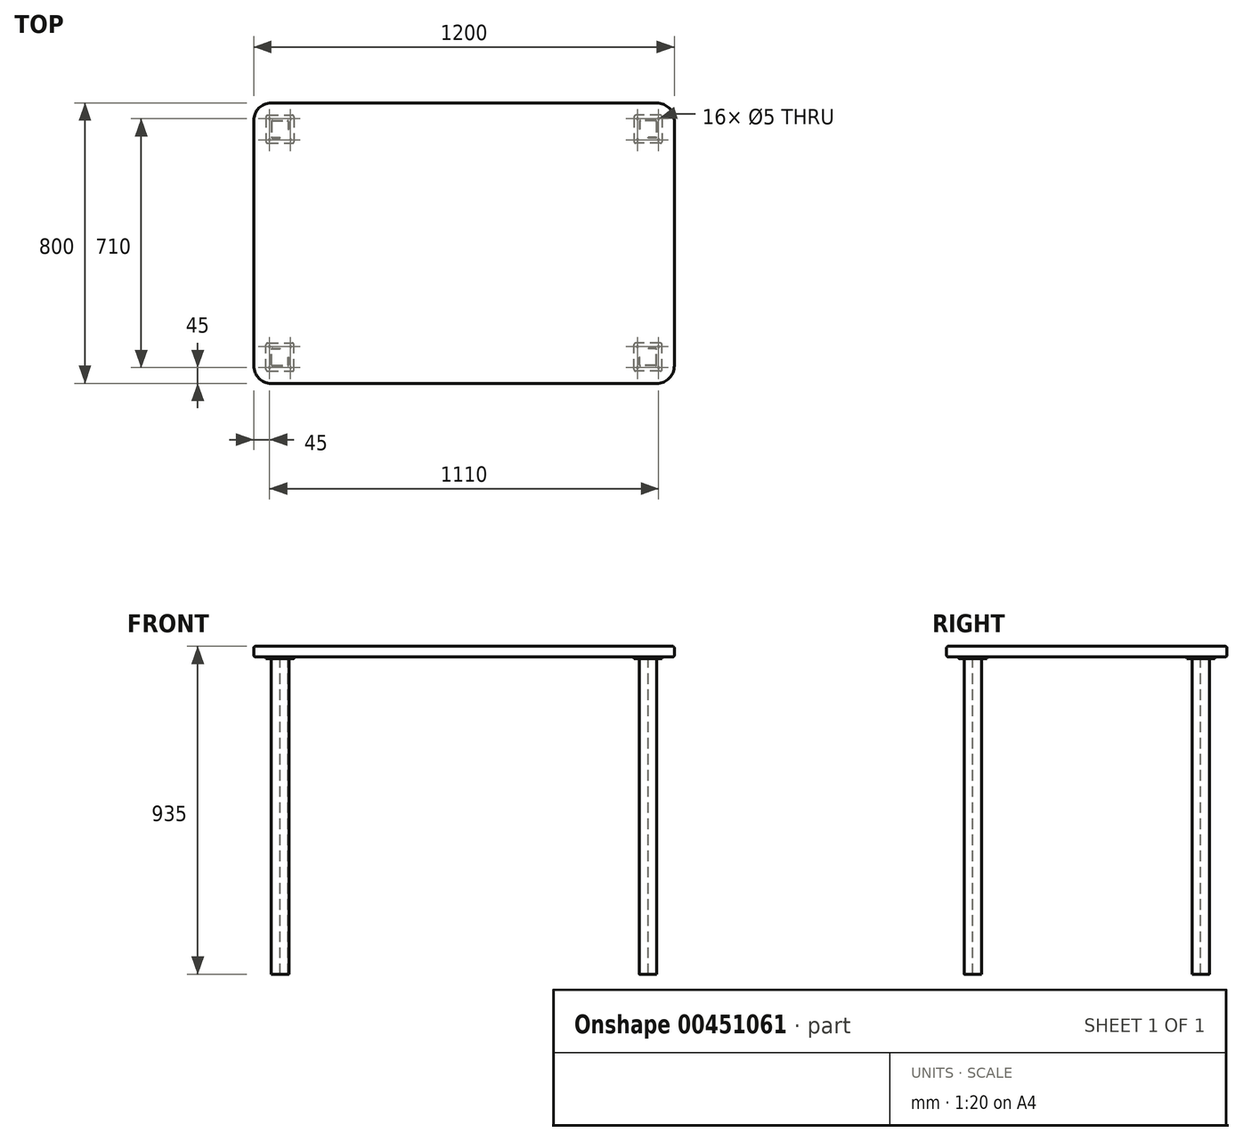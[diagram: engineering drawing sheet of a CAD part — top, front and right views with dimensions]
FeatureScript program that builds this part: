
annotation { "Feature Type Name" : "Feature", "Feature Type Description" : "" }
export const myFeature = defineFeature(function(context is Context, id is Id, definition is map)
    precondition{}
    {
        {
            var Q0;
            Q0=qCreatedBy(makeId("Top.planeOp"),FACE);
            cPlane(context, id + "F0", {"entities" : qUnion([Q0]), "cplaneType" : CPlaneType.OFFSET, "offset" : 5 * mm, "oppositeDirection" : true, "width" : 150 * mm, "height" : 150 * mm});
        }
        {
            var Q0;
            Q0=qCreatedBy(id+"F0.planeOp",FACE);
            var sketch = newSketch(context, id + "F1", { "sketchPlane" : qUnion([Q0])});
            skLineSegment(sketch, "E0.bottom", {"start": v(-546.5, -350) * mm, "end": v(-503.5, -350) * mm});
            skLineSegment(sketch, "E0.top", {"start": v(-546.5, -300) * mm, "end": v(-525, -300) * mm});
            skLineSegment(sketch, "E0.left", {"start": v(-550, -346.5) * mm, "end": v(-550, -303.5) * mm});
            skLineSegment(sketch, "E0.right", {"start": v(-500, -346.5) * mm, "end": v(-500, -325) * mm});
            skPoint(sketch, "E1.endSnap0", {"position": v(-500, -325) * mm});
            skPoint(sketch, "E2.orphan", {"position": v(-500, -300) * mm});
            skPoint(sketch, "E1.start.orphan", {"position": v(-500, -325) * mm});
            skPoint(sketch, "E3.visualSharp", {"position": v(-550, -300) * mm});
            skArc(sketch, "E3.filletArc", {"start": v(-546.5, -300) * mm, "mid": v(-548.97, -301.03) * mm, "end": v(-550, -303.5) * mm});
            skPoint(sketch, "E4.visualSharp", {"position": v(-500, -350) * mm});
            skArc(sketch, "E4.filletArc", {"start": v(-503.5, -350) * mm, "mid": v(-501.03, -348.97) * mm, "end": v(-500, -346.5) * mm});
            skArc(sketch, "E5.filletArc", {"start": v(-550, -346.5) * mm, "mid": v(-548.97, -348.97) * mm, "end": v(-546.5, -350) * mm});
            skLineSegment(sketch, "E6.0", {"start": v(-546.5, -301.5) * mm, "end": v(-525, -301.5) * mm});
            skArc(sketch, "E6.1", {"start": v(-546.5, -301.5) * mm, "mid": v(-547.91, -302.09) * mm, "end": v(-548.5, -303.5) * mm});
            skLineSegment(sketch, "E6.2", {"start": v(-548.5, -346.5) * mm, "end": v(-548.5, -303.5) * mm});
            skLineSegment(sketch, "E6.3", {"start": v(-501.5, -346.5) * mm, "end": v(-501.5, -325) * mm});
            skArc(sketch, "E6.4", {"start": v(-503.5, -348.5) * mm, "mid": v(-502.09, -347.91) * mm, "end": v(-501.5, -346.5) * mm});
            skLineSegment(sketch, "E6.5", {"start": v(-546.5, -348.5) * mm, "end": v(-503.5, -348.5) * mm});
            skArc(sketch, "E6.6", {"start": v(-548.5, -346.5) * mm, "mid": v(-547.91, -347.91) * mm, "end": v(-546.5, -348.5) * mm});
            skLineSegment(sketch, "E7", {"start": v(-525, -300) * mm, "end": v(-525, -301.5) * mm});
            skLineSegment(sketch, "E8", {"start": v(-501.5, -325) * mm, "end": v(-500, -325) * mm});
            skSolve(sketch);
        }
        {
            var Q0;
            Q0 = qSketchRegion(id + "F1", true);
            extrude(context, id + "F2", {"entities" : qUnion([Q0]), "oppositeDirection" : true, "depth" : 900 * mm});
        }
        {
            var Q0;
            Q0=makeQuery(id+"F2.opExtrude","CAP_FACE",FACE,{"disambiguationData":[OSD([sQuery(id+"F1.wireOp",EDGE,"E0.bottom"),sQuery(id+"F1.wireOp",EDGE,"E0.top"),sQuery(id+"F1.wireOp",EDGE,"E0.left"),sQuery(id+"F1.wireOp",EDGE,"E0.right"),sQuery(id+"F1.wireOp",EDGE,"E3.filletArc"),sQuery(id+"F1.wireOp",EDGE,"E4.filletArc"),sQuery(id+"F1.wireOp",EDGE,"E5.filletArc"),sQuery(id+"F1.wireOp",EDGE,"E6.0"),sQuery(id+"F1.wireOp",EDGE,"E6.1"),sQuery(id+"F1.wireOp",EDGE,"E6.2"),sQuery(id+"F1.wireOp",EDGE,"E6.3"),sQuery(id+"F1.wireOp",EDGE,"E6.4"),sQuery(id+"F1.wireOp",EDGE,"E6.5"),sQuery(id+"F1.wireOp",EDGE,"E6.6"),sQuery(id+"F1.wireOp",EDGE,"E7"),sQuery(id+"F1.wireOp",EDGE,"E8")])],"isStart":true});
            var sketch = newSketch(context, id + "F3", { "sketchPlane" : qUnion([Q0])});
            skLineSegment(sketch, "E9.0", {"start": v(-565, -285) * mm, "end": v(-485, -285) * mm});
            skLineSegment(sketch, "E9.2", {"start": v(-565, -365) * mm, "end": v(-565, -285) * mm});
            skLineSegment(sketch, "E9.3", {"start": v(-485, -365) * mm, "end": v(-485, -285) * mm});
            skLineSegment(sketch, "E9.5", {"start": v(-565, -365) * mm, "end": v(-485, -365) * mm});
            skSolve(sketch);
        }
        {
            var Q0;
            Q0 = qSketchRegion(id + "F3", true);
            extrude(context, id + "F4", {"entities" : qUnion([Q0]), "depth" : 5 * mm});
        }
        {
            var Q0;
            Q0=makeQuery(id+"F4.opExtrude","SWEPT_EDGE",EDGE,{"disambiguationData":[OSD([sQuery(id+"F3.wireOp",EDGE,"E9.0"),sQuery(id+"F3.wireOp",EDGE,"E9.2")])]});
            var Q1;
            Q1=makeQuery(id+"F4.opExtrude","SWEPT_EDGE",EDGE,{"disambiguationData":[OSD([sQuery(id+"F3.wireOp",EDGE,"E9.2"),sQuery(id+"F3.wireOp",EDGE,"E9.5")])]});
            var Q2;
            Q2=makeQuery(id+"F4.opExtrude","SWEPT_EDGE",EDGE,{"disambiguationData":[OSD([sQuery(id+"F3.wireOp",EDGE,"E9.3"),sQuery(id+"F3.wireOp",EDGE,"E9.5")])]});
            var Q3;
            Q3=makeQuery(id+"F4.opExtrude","SWEPT_EDGE",EDGE,{"disambiguationData":[OSD([sQuery(id+"F3.wireOp",EDGE,"E9.0"),sQuery(id+"F3.wireOp",EDGE,"E9.3")])]});
            fillet(context, id + "F5", {"entities" : qUnion([Q0, Q1, Q2, Q3]), "radius" : 5 * mm, "tangentPropagation" : true, "allowEdgeOverflow" : false});
        }
        {
            var Q0;
            Q0=makeQuery(id+"F4.opExtrude","CAP_FACE",FACE,{"disambiguationData":[OSD([sQuery(id+"F3.wireOp",EDGE,"E9.0"),sQuery(id+"F3.wireOp",EDGE,"E9.2"),sQuery(id+"F3.wireOp",EDGE,"E9.3"),sQuery(id+"F3.wireOp",EDGE,"E9.5")])],"isStart":false});
            var sketch = newSketch(context, id + "F6", { "sketchPlane" : qUnion([Q0])});
            skLineSegment(sketch, "E10.0", {"start": v(-555, -295) * mm, "end": v(-555, -355) * mm, "construction": true});
            skLineSegment(sketch, "E10.1", {"start": v(-495, -295) * mm, "end": v(-555, -295) * mm, "construction": true});
            skLineSegment(sketch, "E10.2", {"start": v(-495, -355) * mm, "end": v(-495, -295) * mm, "construction": true});
            skLineSegment(sketch, "E10.3", {"start": v(-555, -355) * mm, "end": v(-495, -355) * mm, "construction": true});
            skPoint(sketch, "E11", {"position": v(-555, -355) * mm});
            skPoint(sketch, "E12", {"position": v(-495, -355) * mm});
            skPoint(sketch, "E13", {"position": v(-495, -295) * mm});
            skPoint(sketch, "E14", {"position": v(-555, -295) * mm});
            skSolve(sketch);
        }
        {
            var Q0;
            Q0=sQuery(id+"F6.wireOp",VERTEX,"E11");
            var Q1;
            Q1=sQuery(id+"F6.wireOp",VERTEX,"E12");
            var Q2;
            Q2=sQuery(id+"F6.wireOp",VERTEX,"E13");
            var Q3;
            Q3=sQuery(id+"F6.wireOp",VERTEX,"E14");
            var Q4;
            Q4=makeQuery(id+"F4.opExtrude","SWEPT_BODY",BODY,{"disambiguationData":[OSD([sQuery(id+"F3.wireOp",EDGE,"E9.0"),sQuery(id+"F3.wireOp",EDGE,"E9.2"),sQuery(id+"F3.wireOp",EDGE,"E9.3"),sQuery(id+"F3.wireOp",EDGE,"E9.5")])]});
            hole(context, id + "F7", {"style" : HoleStyle.SIMPLE, "endStyle" : HoleEndStyle.THROUGH, "standardTappedOrClearance" : lookupTablePath({ "standard" : "ISO", "size" : "5", "type" : "Drilled" }), "standardBlindInLast" : lookupTablePath({ "standard" : "ISO", "size" : "5", "type" : "Drilled" }), "holeDiameter" : 5 * mm, "isTappedThrough" : true, "tappedDepth" : 12 * mm, "tapClearance" : 3, "locations" : qUnion([Q0, Q1, Q2, Q3]), "scope" : qUnion([Q4])});
        }
        {
            var Q0;
            Q0=makeQuery(id+"F2.opExtrude","SWEPT_BODY",BODY,{"disambiguationData":[OSD([sQuery(id+"F1.wireOp",EDGE,"E0.bottom"),sQuery(id+"F1.wireOp",EDGE,"E0.top"),sQuery(id+"F1.wireOp",EDGE,"E0.left"),sQuery(id+"F1.wireOp",EDGE,"E0.right"),sQuery(id+"F1.wireOp",EDGE,"E3.filletArc"),sQuery(id+"F1.wireOp",EDGE,"E4.filletArc"),sQuery(id+"F1.wireOp",EDGE,"E5.filletArc"),sQuery(id+"F1.wireOp",EDGE,"E6.0"),sQuery(id+"F1.wireOp",EDGE,"E6.1"),sQuery(id+"F1.wireOp",EDGE,"E6.2"),sQuery(id+"F1.wireOp",EDGE,"E6.3"),sQuery(id+"F1.wireOp",EDGE,"E6.4"),sQuery(id+"F1.wireOp",EDGE,"E6.5"),sQuery(id+"F1.wireOp",EDGE,"E6.6"),sQuery(id+"F1.wireOp",EDGE,"E7"),sQuery(id+"F1.wireOp",EDGE,"E8")])]});
            var Q1;
            Q1=makeQuery(id+"F4.opExtrude","SWEPT_BODY",BODY,{"disambiguationData":[OSD([sQuery(id+"F3.wireOp",EDGE,"E9.0"),sQuery(id+"F3.wireOp",EDGE,"E9.2"),sQuery(id+"F3.wireOp",EDGE,"E9.3"),sQuery(id+"F3.wireOp",EDGE,"E9.5")])]});
            var Q2;
            Q2=qCreatedBy(makeId("Front.planeOp"),FACE);
            mirror(context, id + "F8", {"entities" : qUnion([Q0, Q1]), "mirrorPlane" : qUnion([Q2])});
        }
        {
            var Q0;
            Q0=makeQuery(id+"F8.opPattern","COPY",BODY,{"derivedFrom":makeQuery(id+"F2.opExtrude","SWEPT_BODY",BODY,{"disambiguationData":[OSD([sQuery(id+"F1.wireOp",EDGE,"E0.bottom"),sQuery(id+"F1.wireOp",EDGE,"E0.top"),sQuery(id+"F1.wireOp",EDGE,"E0.left"),sQuery(id+"F1.wireOp",EDGE,"E0.right"),sQuery(id+"F1.wireOp",EDGE,"E3.filletArc"),sQuery(id+"F1.wireOp",EDGE,"E4.filletArc"),sQuery(id+"F1.wireOp",EDGE,"E5.filletArc"),sQuery(id+"F1.wireOp",EDGE,"E6.0"),sQuery(id+"F1.wireOp",EDGE,"E6.1"),sQuery(id+"F1.wireOp",EDGE,"E6.2"),sQuery(id+"F1.wireOp",EDGE,"E6.3"),sQuery(id+"F1.wireOp",EDGE,"E6.4"),sQuery(id+"F1.wireOp",EDGE,"E6.5"),sQuery(id+"F1.wireOp",EDGE,"E6.6"),sQuery(id+"F1.wireOp",EDGE,"E7"),sQuery(id+"F1.wireOp",EDGE,"E8")])]}),"instanceName":"1"});
            var Q1;
            Q1=makeQuery(id+"F2.opExtrude","SWEPT_BODY",BODY,{"disambiguationData":[OSD([sQuery(id+"F1.wireOp",EDGE,"E0.bottom"),sQuery(id+"F1.wireOp",EDGE,"E0.top"),sQuery(id+"F1.wireOp",EDGE,"E0.left"),sQuery(id+"F1.wireOp",EDGE,"E0.right"),sQuery(id+"F1.wireOp",EDGE,"E3.filletArc"),sQuery(id+"F1.wireOp",EDGE,"E4.filletArc"),sQuery(id+"F1.wireOp",EDGE,"E5.filletArc"),sQuery(id+"F1.wireOp",EDGE,"E6.0"),sQuery(id+"F1.wireOp",EDGE,"E6.1"),sQuery(id+"F1.wireOp",EDGE,"E6.2"),sQuery(id+"F1.wireOp",EDGE,"E6.3"),sQuery(id+"F1.wireOp",EDGE,"E6.4"),sQuery(id+"F1.wireOp",EDGE,"E6.5"),sQuery(id+"F1.wireOp",EDGE,"E6.6"),sQuery(id+"F1.wireOp",EDGE,"E7"),sQuery(id+"F1.wireOp",EDGE,"E8")])]});
            var Q2;
            Q2=makeQuery(id+"F8.opPattern","COPY",BODY,{"derivedFrom":makeQuery(id+"F4.opExtrude","SWEPT_BODY",BODY,{"disambiguationData":[OSD([sQuery(id+"F3.wireOp",EDGE,"E9.0"),sQuery(id+"F3.wireOp",EDGE,"E9.2"),sQuery(id+"F3.wireOp",EDGE,"E9.3"),sQuery(id+"F3.wireOp",EDGE,"E9.5")])]}),"instanceName":"1"});
            var Q3;
            Q3=makeQuery(id+"F4.opExtrude","SWEPT_BODY",BODY,{"disambiguationData":[OSD([sQuery(id+"F3.wireOp",EDGE,"E9.0"),sQuery(id+"F3.wireOp",EDGE,"E9.2"),sQuery(id+"F3.wireOp",EDGE,"E9.3"),sQuery(id+"F3.wireOp",EDGE,"E9.5")])]});
            var Q4;
            Q4=qCreatedBy(makeId("Right.planeOp"),FACE);
            mirror(context, id + "F9", {"entities" : qUnion([Q0, Q1, Q2, Q3]), "mirrorPlane" : qUnion([Q4])});
        }
        {
            var Q0;
            Q0=qCreatedBy(makeId("Top.planeOp"),FACE);
            var sketch = newSketch(context, id + "F10", { "sketchPlane" : qUnion([Q0])});
            skLineSegment(sketch, "E15.bottom", {"start": v(-600, 400) * mm, "end": v(600, 400) * mm});
            skLineSegment(sketch, "E15.top", {"start": v(-600, -400) * mm, "end": v(600, -400) * mm});
            skLineSegment(sketch, "E15.left", {"start": v(-600, 400) * mm, "end": v(-600, -400) * mm});
            skLineSegment(sketch, "E15.right", {"start": v(600, 400) * mm, "end": v(600, -400) * mm});
            skPoint(sketch, "E15.middle", {"position": v(0, 0) * mm});
            skSolve(sketch);
        }
        {
            var Q0;
            Q0 = qSketchRegion(id + "F10", true);
            extrude(context, id + "F11", {"entities" : qUnion([Q0]), "depth" : 30 * mm});
        }
        {
            var Q0;
            Q0=makeQuery(id+"F11.opExtrude","SWEPT_EDGE",EDGE,{"disambiguationData":[OSD([sQuery(id+"F10.wireOp",EDGE,"E15.top"),sQuery(id+"F10.wireOp",EDGE,"E15.right")])]});
            var Q1;
            Q1=makeQuery(id+"F11.opExtrude","SWEPT_EDGE",EDGE,{"disambiguationData":[OSD([sQuery(id+"F10.wireOp",EDGE,"E15.top"),sQuery(id+"F10.wireOp",EDGE,"E15.left")])]});
            var Q2;
            Q2=makeQuery(id+"F11.opExtrude","SWEPT_EDGE",EDGE,{"disambiguationData":[OSD([sQuery(id+"F10.wireOp",EDGE,"E15.bottom"),sQuery(id+"F10.wireOp",EDGE,"E15.left")])]});
            var Q3;
            Q3=makeQuery(id+"F11.opExtrude","SWEPT_EDGE",EDGE,{"disambiguationData":[OSD([sQuery(id+"F10.wireOp",EDGE,"E15.bottom"),sQuery(id+"F10.wireOp",EDGE,"E15.right")])]});
            fillet(context, id + "F12", {"entities" : qUnion([Q0, Q1, Q2, Q3]), "radius" : 50 * mm, "tangentPropagation" : true, "allowEdgeOverflow" : false});
        }
        {
            var Q0;
            Q0=makeQuery(id+"F11.opExtrude","CAP_FACE",FACE,{"disambiguationData":[OSD([sQuery(id+"F10.wireOp",EDGE,"E15.bottom"),sQuery(id+"F10.wireOp",EDGE,"E15.top"),sQuery(id+"F10.wireOp",EDGE,"E15.left"),sQuery(id+"F10.wireOp",EDGE,"E15.right")])],"isStart":false});
            var Q1;
            Q1=makeQuery(id+"F11.opExtrude","CAP_FACE",FACE,{"disambiguationData":[OSD([sQuery(id+"F10.wireOp",EDGE,"E15.bottom"),sQuery(id+"F10.wireOp",EDGE,"E15.top"),sQuery(id+"F10.wireOp",EDGE,"E15.left"),sQuery(id+"F10.wireOp",EDGE,"E15.right")])],"isStart":true});
            fillet(context, id + "F13", {"entities" : qUnion([Q0, Q1]), "radius" : 5 * mm, "tangentPropagation" : true, "allowEdgeOverflow" : false});
        }
    });
